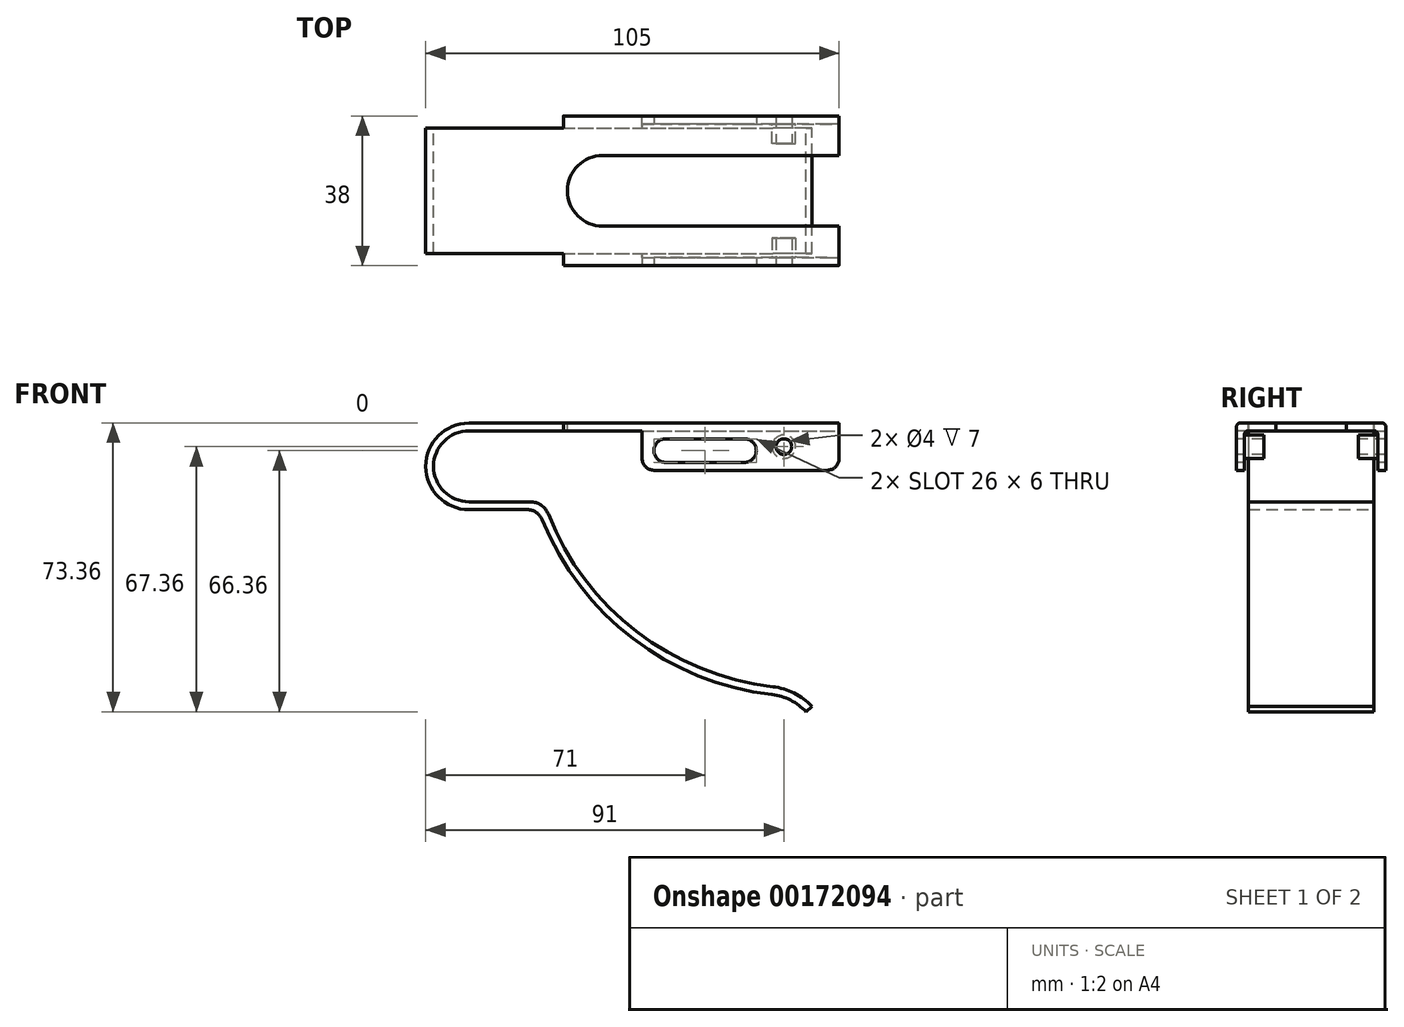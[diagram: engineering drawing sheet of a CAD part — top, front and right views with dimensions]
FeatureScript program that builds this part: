
annotation { "Feature Type Name" : "Feature", "Feature Type Description" : "" }
export const myFeature = defineFeature(function(context is Context, id is Id, definition is map)
    precondition{}
    {
        {
            var Q0;
            Q0=qCreatedBy(makeId("Front.planeOp"),FACE);
            var sketch = newSketch(context, id + "F0", { "sketchPlane" : qUnion([Q0])});
            skArc(sketch, "E0", {"start": v(0, 9) * mm, "mid": v(-9, 0) * mm, "end": v(0, -9) * mm});
            skLineSegment(sketch, "E1", {"start": v(0, 9) * mm, "end": v(94, 9) * mm});
            skLineSegment(sketch, "E2", {"start": v(0, -9) * mm, "end": v(15.51, -9) * mm});
            skArc(sketch, "E3", {"start": v(20.16, -12.16) * mm, "mid": v(42.63, -41.98) * mm, "end": v(77.22, -56) * mm});
            skArc(sketch, "E4", {"start": v(87.1, -61) * mm, "mid": v(82.61, -57.62) * mm, "end": v(77.22, -56) * mm});
            skPoint(sketch, "E5.visualSharp", {"position": v(19, -9) * mm});
            skArc(sketch, "E5.filletArc", {"start": v(20.16, -12.16) * mm, "mid": v(18.32, -9.87) * mm, "end": v(15.51, -9) * mm});
            skArc(sketch, "E6.0", {"start": v(85.64, -62.36) * mm, "mid": v(81.71, -59.4) * mm, "end": v(77, -57.99) * mm});
            skLineSegment(sketch, "E6.1", {"start": v(0, 11) * mm, "end": v(94, 11) * mm});
            skArc(sketch, "E6.2", {"start": v(0, 11) * mm, "mid": v(-11, 0) * mm, "end": v(0, -11) * mm});
            skLineSegment(sketch, "E6.3", {"start": v(0, -11) * mm, "end": v(14.83, -11) * mm});
            skArc(sketch, "E6.4", {"start": v(18.54, -13.5) * mm, "mid": v(41.67, -43.76) * mm, "end": v(77, -57.99) * mm});
            skLineSegment(sketch, "E7", {"start": v(94, 11) * mm, "end": v(94, 9) * mm});
            skLineSegment(sketch, "E8", {"start": v(85.64, -62.36) * mm, "end": v(87.1, -61) * mm});
            skPoint(sketch, "E9.visualSharp", {"position": v(17.58, -11) * mm});
            skArc(sketch, "E9.filletArc", {"start": v(18.54, -13.5) * mm, "mid": v(17.07, -11.68) * mm, "end": v(14.83, -11) * mm});
            skSolve(sketch);
        }
        {
            var Q0;
            Q0 = qSketchRegion(id + "F0", true);
            extrude(context, id + "F1", {"entities" : qUnion([Q0]), "depth" : 16 * mm});
        }
        {
            var Q0;
            Q0=makeQuery(id+"F1.opExtrude","SWEPT_FACE",FACE,{"disambiguationData":[OSD([sQuery(id+"F0.wireOp",EDGE,"E6.1")])]});
            var sketch = newSketch(context, id + "F2", { "sketchPlane" : qUnion([Q0])});
            skLineSegment(sketch, "E10.bottom", {"start": v(24, -16) * mm, "end": v(94, -16) * mm});
            skLineSegment(sketch, "E10.top", {"start": v(24, -19) * mm, "end": v(94, -19) * mm});
            skLineSegment(sketch, "E10.left", {"start": v(24, -16) * mm, "end": v(24, -19) * mm});
            skLineSegment(sketch, "E10.right", {"start": v(94, -16) * mm, "end": v(94, -19) * mm});
            skSolve(sketch);
        }
        {
            var Q0;
            Q0 = qSketchRegion(id + "F2", true);
            extrude(context, id + "F3", {"entities" : qUnion([Q0]), "operationType" : NewBodyOperationType.ADD, "oppositeDirection" : true, "depth" : 2 * mm});
        }
        {
            var Q0;
            Q0=makeQuery(id+"F3.opExtrude","SWEPT_FACE",FACE,{"disambiguationData":[OSD([sQuery(id+"F2.wireOp",EDGE,"E10.top")])]});
            var sketch = newSketch(context, id + "F4", { "sketchPlane" : qUnion([Q0])});
            skLineSegment(sketch, "E11.bottom", {"start": v(94, 11) * mm, "end": v(44, 11) * mm});
            skLineSegment(sketch, "E11.top", {"start": v(94, -1) * mm, "end": v(44, -1) * mm});
            skLineSegment(sketch, "E11.left", {"start": v(94, 11) * mm, "end": v(94, -1) * mm});
            skLineSegment(sketch, "E11.right", {"start": v(44, 11) * mm, "end": v(44, -1) * mm});
            skSolve(sketch);
        }
        {
            var Q0;
            Q0 = qSketchRegion(id + "F4", true);
            extrude(context, id + "F5", {"entities" : qUnion([Q0]), "operationType" : NewBodyOperationType.ADD, "oppositeDirection" : true, "depth" : 2 * mm});
        }
        {
            var Q0;
            Q0=makeQuery(id+"F3.opExtrude","CAP_EDGE",EDGE,{"disambiguationData":[OSD([sQuery(id+"F2.wireOp",EDGE,"E10.top")])],"isStart":true});
            var Q1;
            Q1=makeQuery(id+"F5.boolean.opBoolean","INTERSECT",EDGE,{"derivedFrom":[makeQuery(id+"F3.boolean.opBoolean","MERGE",FACE,{"derivedFrom":[makeQuery(id+"F1.opExtrude","SWEPT_FACE",FACE,{"disambiguationData":[OSD([sQuery(id+"F0.wireOp",EDGE,"E1")])]}),makeQuery(id+"F3.opExtrude","CAP_FACE",FACE,{"disambiguationData":[OSD([sQuery(id+"F2.wireOp",EDGE,"E10.bottom"),sQuery(id+"F2.wireOp",EDGE,"E10.top"),sQuery(id+"F2.wireOp",EDGE,"E10.left"),sQuery(id+"F2.wireOp",EDGE,"E10.right")])],"isStart":false})]}),makeQuery(id+"F5.opExtrude","CAP_FACE",FACE,{"disambiguationData":[OSD([sQuery(id+"F4.wireOp",EDGE,"E11.bottom"),sQuery(id+"F4.wireOp",EDGE,"E11.top"),sQuery(id+"F4.wireOp",EDGE,"E11.left"),sQuery(id+"F4.wireOp",EDGE,"E11.right")])],"isStart":false})]});
            fillet(context, id + "F6", {"entities" : qUnion([Q0, Q1]), "radius" : 1 * mm, "allowEdgeOverflow" : false});
        }
        {
            var Q0;
            Q0=makeQuery(id+"F1.opExtrude","SWEPT_BODY",BODY,{"disambiguationData":[OSD([sQuery(id+"F0.wireOp",EDGE,"E0"),sQuery(id+"F0.wireOp",EDGE,"E1"),sQuery(id+"F0.wireOp",EDGE,"E2"),sQuery(id+"F0.wireOp",EDGE,"E3"),sQuery(id+"F0.wireOp",EDGE,"E4"),sQuery(id+"F0.wireOp",EDGE,"E5.filletArc"),sQuery(id+"F0.wireOp",EDGE,"E6.0"),sQuery(id+"F0.wireOp",EDGE,"E6.1"),sQuery(id+"F0.wireOp",EDGE,"E6.2"),sQuery(id+"F0.wireOp",EDGE,"E6.3"),sQuery(id+"F0.wireOp",EDGE,"E6.4"),sQuery(id+"F0.wireOp",EDGE,"E7"),sQuery(id+"F0.wireOp",EDGE,"E8"),sQuery(id+"F0.wireOp",EDGE,"E9.filletArc")])]});
            var Q1;
            Q1=qCreatedBy(makeId("Front.planeOp"),FACE);
            mirror(context, id + "F7", {"operationType" : NewBodyOperationType.ADD, "entities" : qUnion([Q0]), "mirrorPlane" : qUnion([Q1])});
        }
        {
            var Q0;
            {var subQ0=makeQuery(id+"F3.boolean.opBoolean","MERGE",FACE,{"derivedFrom":[makeQuery(id+"F1.opExtrude","SWEPT_FACE",FACE,{"disambiguationData":[OSD([sQuery(id+"F0.wireOp",EDGE,"E6.1")])]}),makeQuery(id+"F3.opExtrude","CAP_FACE",FACE,{"disambiguationData":[OSD([sQuery(id+"F2.wireOp",EDGE,"E10.bottom"),sQuery(id+"F2.wireOp",EDGE,"E10.top"),sQuery(id+"F2.wireOp",EDGE,"E10.left"),sQuery(id+"F2.wireOp",EDGE,"E10.right")])],"isStart":true})]});Q0=makeQuery(id+"F7.boolean.opBoolean","MERGE",FACE,{"derivedFrom":[subQ0,makeQuery(id+"F7.opPattern","COPY",FACE,{"derivedFrom":subQ0,"instanceName":"1"})]});}
            var sketch = newSketch(context, id + "F8", { "sketchPlane" : qUnion([Q0])});
            skArc(sketch, "E12", {"start": v(34, 8.99) * mm, "mid": v(25.01, 0) * mm, "end": v(34, -8.99) * mm});
            skLineSegment(sketch, "E13", {"start": v(34, 8.99) * mm, "end": v(94, 8.99) * mm});
            skLineSegment(sketch, "E14", {"start": v(34, -8.99) * mm, "end": v(94, -8.99) * mm});
            skLineSegment(sketch, "E15", {"start": v(94, -8.99) * mm, "end": v(94, 8.99) * mm});
            skSolve(sketch);
        }
        {
            var Q0;
            Q0 = qSketchRegion(id + "F8", true);
            extrude(context, id + "F9", {"entities" : qUnion([Q0]), "operationType" : NewBodyOperationType.REMOVE, "oppositeDirection" : true, "depth" : 2 * mm});
        }
        {
            var Q0;
            Q0=makeQuery(id+"F5.boolean.opBoolean","MERGE",FACE,{"derivedFrom":[makeQuery(id+"F3.opExtrude","SWEPT_FACE",FACE,{"disambiguationData":[OSD([sQuery(id+"F2.wireOp",EDGE,"E10.top")])]}),makeQuery(id+"F5.opExtrude","CAP_FACE",FACE,{"disambiguationData":[OSD([sQuery(id+"F4.wireOp",EDGE,"E11.bottom"),sQuery(id+"F4.wireOp",EDGE,"E11.top"),sQuery(id+"F4.wireOp",EDGE,"E11.left"),sQuery(id+"F4.wireOp",EDGE,"E11.right")])],"isStart":true})]});
            var sketch = newSketch(context, id + "F10", { "sketchPlane" : qUnion([Q0])});
            skLineSegment(sketch, "E16", {"start": v(50, 4) * mm, "end": v(70, 4) * mm});
            skPoint(sketch, "E16.startSnap0", {"position": v(44, 4) * mm});
            skArc(sketch, "E17.0.startCap", {"start": v(50, 1) * mm, "mid": v(47, 4) * mm, "end": v(50, 7) * mm});
            skArc(sketch, "E17.0.endCap", {"start": v(70, 7) * mm, "mid": v(73, 4) * mm, "end": v(70, 1) * mm});
            skLineSegment(sketch, "E17.0.left", {"start": v(50, 7) * mm, "end": v(70, 7) * mm});
            skLineSegment(sketch, "E17.0.right", {"start": v(50, 1) * mm, "end": v(70, 1) * mm});
            skSolve(sketch);
        }
        {
            var Q0;
            Q0 = qSketchRegion(id + "F10", true);
            extrude(context, id + "F11", {"entities" : qUnion([Q0]), "operationType" : NewBodyOperationType.REMOVE, "endBound" : BoundingType.THROUGH_ALL, "oppositeDirection" : true, "depth" : 25 * mm});
        }
        {
            var Q0;
            Q0=makeQuery(id+"F5.boolean.opBoolean","MERGE",FACE,{"derivedFrom":[makeQuery(id+"F3.opExtrude","SWEPT_FACE",FACE,{"disambiguationData":[OSD([sQuery(id+"F2.wireOp",EDGE,"E10.top")])]}),makeQuery(id+"F5.opExtrude","CAP_FACE",FACE,{"disambiguationData":[OSD([sQuery(id+"F4.wireOp",EDGE,"E11.bottom"),sQuery(id+"F4.wireOp",EDGE,"E11.top"),sQuery(id+"F4.wireOp",EDGE,"E11.left"),sQuery(id+"F4.wireOp",EDGE,"E11.right")])],"isStart":true})]});
            var sketch = newSketch(context, id + "F12", { "sketchPlane" : qUnion([Q0])});
            skPoint(sketch, "E18", {"position": v(80, 5) * mm});
            skSolve(sketch);
        }
        {
            var Q0;
            Q0=sQuery(id+"F12.wireOp",VERTEX,"E18");
            var Q1;
            Q1=makeQuery(id+"F1.opExtrude","SWEPT_BODY",BODY,{"disambiguationData":[OSD([sQuery(id+"F0.wireOp",EDGE,"E0"),sQuery(id+"F0.wireOp",EDGE,"E1"),sQuery(id+"F0.wireOp",EDGE,"E2"),sQuery(id+"F0.wireOp",EDGE,"E3"),sQuery(id+"F0.wireOp",EDGE,"E4"),sQuery(id+"F0.wireOp",EDGE,"E5.filletArc"),sQuery(id+"F0.wireOp",EDGE,"E6.0"),sQuery(id+"F0.wireOp",EDGE,"E6.1"),sQuery(id+"F0.wireOp",EDGE,"E6.2"),sQuery(id+"F0.wireOp",EDGE,"E6.3"),sQuery(id+"F0.wireOp",EDGE,"E6.4"),sQuery(id+"F0.wireOp",EDGE,"E7"),sQuery(id+"F0.wireOp",EDGE,"E8"),sQuery(id+"F0.wireOp",EDGE,"E9.filletArc")])]});
            hole(context, id + "F13", {"style" : HoleStyle.SIMPLE, "endStyle" : HoleEndStyle.THROUGH, "holeDiameter" : 4 * mm, "locations" : qUnion([Q0]), "scope" : qUnion([Q1]), "isTappedThrough" : true});
        }
        {
            var Q0;
            Q0=makeQuery(id+"F5.opExtrude","CAP_FACE",FACE,{"disambiguationData":[OSD([sQuery(id+"F4.wireOp",EDGE,"E11.bottom"),sQuery(id+"F4.wireOp",EDGE,"E11.top"),sQuery(id+"F4.wireOp",EDGE,"E11.left"),sQuery(id+"F4.wireOp",EDGE,"E11.right")])],"isStart":false});
            var sketch = newSketch(context, id + "F14", { "sketchPlane" : qUnion([Q0])});
            skCircle(sketch, "E19.0", {"center": v(-80, 5) * mm, "radius": 2 * mm});
            skCircle(sketch, "E20.0", {"center": v(-80, 5) * mm, "radius": 3 * mm});
            skSolve(sketch);
        }
        {
            var Q0;
            Q0 = qSketchRegion(id + "F14", true);
            extrude(context, id + "F15", {"entities" : qUnion([Q0]), "operationType" : NewBodyOperationType.ADD, "depth" : 5 * mm});
        }
        {
            var Q0;
            Q0=makeQuery(id+"F7.opPattern","COPY",FACE,{"derivedFrom":makeQuery(id+"F5.opExtrude","CAP_FACE",FACE,{"disambiguationData":[OSD([sQuery(id+"F4.wireOp",EDGE,"E11.bottom"),sQuery(id+"F4.wireOp",EDGE,"E11.top"),sQuery(id+"F4.wireOp",EDGE,"E11.left"),sQuery(id+"F4.wireOp",EDGE,"E11.right")])],"isStart":false}),"instanceName":"1"});
            var sketch = newSketch(context, id + "F16", { "sketchPlane" : qUnion([Q0])});
            skCircle(sketch, "E21.0", {"center": v(80, 5) * mm, "radius": 2 * mm});
            skCircle(sketch, "E22.0", {"center": v(80, 5) * mm, "radius": 3 * mm});
            skSolve(sketch);
        }
        {
            var Q0;
            Q0 = qSketchRegion(id + "F16", true);
            extrude(context, id + "F17", {"entities" : qUnion([Q0]), "operationType" : NewBodyOperationType.ADD, "depth" : 5 * mm});
        }
        {
            var Q0;
            Q0=makeQuery(id+"F7.opPattern","COPY",EDGE,{"derivedFrom":makeQuery(id+"F5.opExtrude","SWEPT_EDGE",EDGE,{"disambiguationData":[OSD([sQuery(id+"F4.wireOp",EDGE,"E11.top"),sQuery(id+"F4.wireOp",EDGE,"E11.left")])]}),"instanceName":"1"});
            var Q1;
            Q1=makeQuery(id+"F5.opExtrude","SWEPT_EDGE",EDGE,{"disambiguationData":[OSD([sQuery(id+"F4.wireOp",EDGE,"E11.top"),sQuery(id+"F4.wireOp",EDGE,"E11.left")])]});
            var Q2;
            Q2=makeQuery(id+"F5.opExtrude","SWEPT_EDGE",EDGE,{"disambiguationData":[OSD([sQuery(id+"F4.wireOp",EDGE,"E11.top"),sQuery(id+"F4.wireOp",EDGE,"E11.right")])]});
            var Q3;
            Q3=makeQuery(id+"F7.opPattern","COPY",EDGE,{"derivedFrom":makeQuery(id+"F5.opExtrude","SWEPT_EDGE",EDGE,{"disambiguationData":[OSD([sQuery(id+"F4.wireOp",EDGE,"E11.top"),sQuery(id+"F4.wireOp",EDGE,"E11.right")])]}),"instanceName":"1"});
            fillet(context, id + "F18", {"entities" : qUnion([Q0, Q1, Q2, Q3]), "radius" : 3 * mm, "tangentPropagation" : true, "allowEdgeOverflow" : false});
        }
    });
